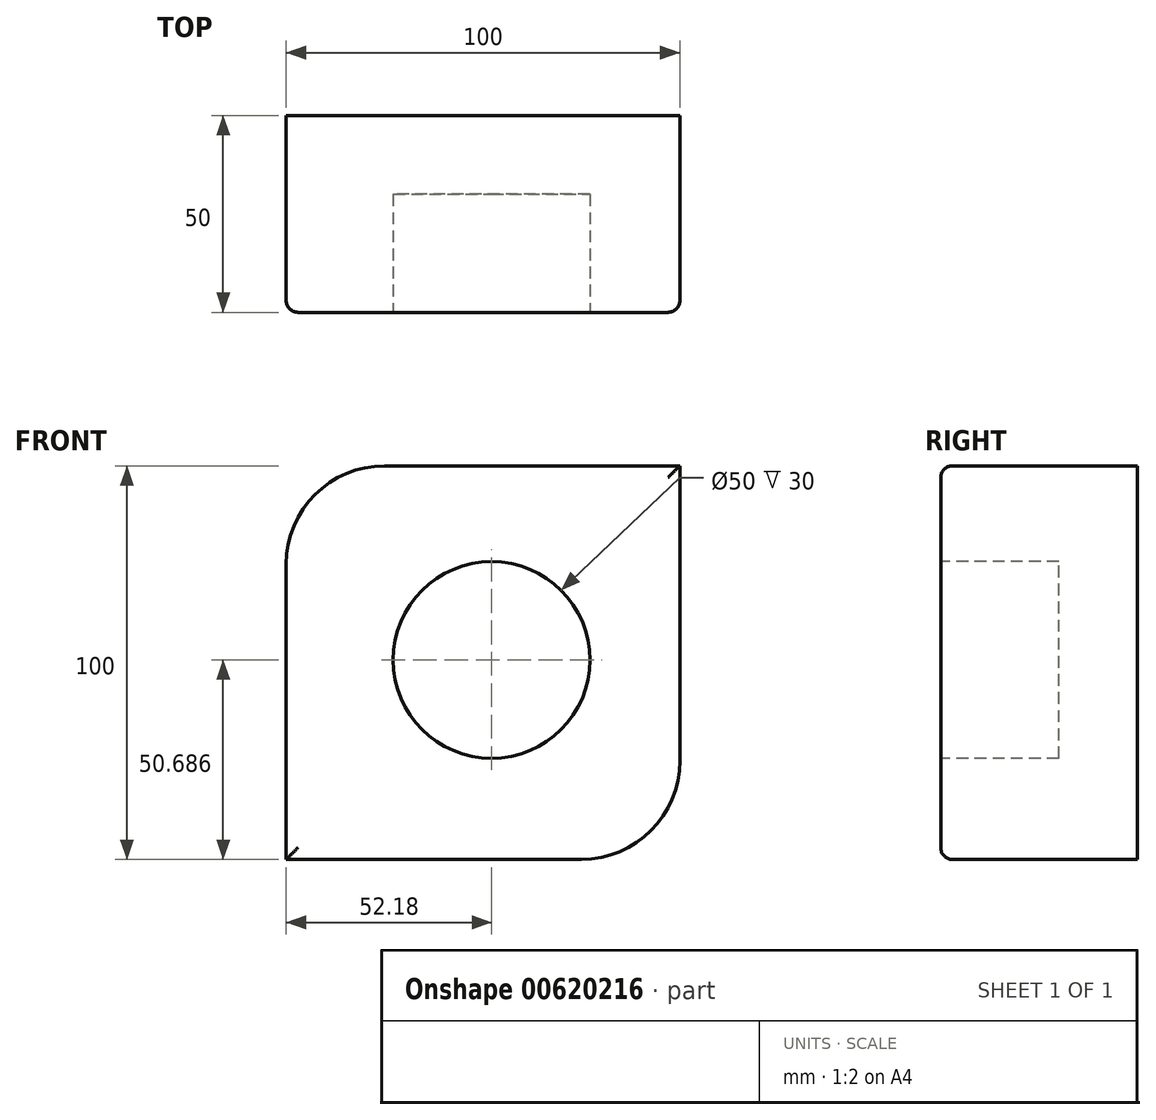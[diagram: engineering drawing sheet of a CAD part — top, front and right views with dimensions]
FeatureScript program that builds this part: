
annotation { "Feature Type Name" : "Feature", "Feature Type Description" : "" }
export const myFeature = defineFeature(function(context is Context, id is Id, definition is map)
    precondition{}
    {
        {
            var Q0;
            Q0=qCreatedBy(makeId("Front.planeOp"),FACE);
            var sketch = newSketch(context, id + "F0", { "sketchPlane" : qUnion([Q0])});
            skLineSegment(sketch, "E0.bottom", {"start": v(-20.42, 67.46) * mm, "end": v(54.58, 67.46) * mm});
            skLineSegment(sketch, "E0.top", {"start": v(-45.42, -32.54) * mm, "end": v(29.58, -32.54) * mm});
            skLineSegment(sketch, "E0.left", {"start": v(-45.42, 42.46) * mm, "end": v(-45.42, -32.54) * mm});
            skLineSegment(sketch, "E0.right", {"start": v(54.58, 67.46) * mm, "end": v(54.58, -7.54) * mm});
            skPoint(sketch, "E1.visualSharp", {"position": v(-45.42, 67.46) * mm});
            skArc(sketch, "E1.filletArc", {"start": v(-20.42, 67.46) * mm, "mid": v(-38.1, 60.14) * mm, "end": v(-45.42, 42.46) * mm});
            skPoint(sketch, "E2.visualSharp", {"position": v(54.58, -32.54) * mm});
            skArc(sketch, "E2.filletArc", {"start": v(29.58, -32.54) * mm, "mid": v(47.25, -25.22) * mm, "end": v(54.58, -7.54) * mm});
            skSolve(sketch);
        }
        {
            var Q0;
            Q0=makeQuery(id+"F0.imprint","IMPRINT",FACE,{"disambiguationData":[TD([[makeQuery(id+"F0.imprint","IMPRINT",EDGE,{"derivedFrom":sQuery(id+"F0.wireOp",EDGE,"E0.bottom")}),-1.0]])]});
            extrude(context, id + "F1", {"entities" : qUnion([Q0]), "depth" : 50 * mm, "offsetDistance" : 25 * mm});
        }
        {
            var Q0;
            Q0=makeQuery(id+"F1.opExtrude","CAP_FACE",FACE,{"disambiguationData":[OSD([sQuery(id+"F0.wireOp",EDGE,"E0.bottom"),sQuery(id+"F0.wireOp",EDGE,"E0.top"),sQuery(id+"F0.wireOp",EDGE,"E0.left"),sQuery(id+"F0.wireOp",EDGE,"E0.right"),sQuery(id+"F0.wireOp",EDGE,"E1.filletArc"),sQuery(id+"F0.wireOp",EDGE,"E2.filletArc")])],"isStart":false});
            fillet(context, id + "F2", {"entities" : qUnion([Q0]), "radius" : 3 * mm, "tangentPropagation" : true, "allowEdgeOverflow" : false});
        }
        {
            var Q0;
            Q0=makeQuery(id+"F1.opExtrude","CAP_FACE",FACE,{"disambiguationData":[OSD([sQuery(id+"F0.wireOp",EDGE,"E0.bottom"),sQuery(id+"F0.wireOp",EDGE,"E0.top"),sQuery(id+"F0.wireOp",EDGE,"E0.left"),sQuery(id+"F0.wireOp",EDGE,"E0.right"),sQuery(id+"F0.wireOp",EDGE,"E1.filletArc"),sQuery(id+"F0.wireOp",EDGE,"E2.filletArc")])],"isStart":false});
            var sketch = newSketch(context, id + "F3", { "sketchPlane" : qUnion([Q0])});
            skCircle(sketch, "E3", {"center": v(6.76, 18.15) * mm, "radius": 25 * mm});
            skSolve(sketch);
        }
        {
            var Q0;
            Q0=makeQuery(id+"F3.imprint","IMPRINT",FACE,{"disambiguationData":[TD([[makeQuery(id+"F3.imprint","IMPRINT",EDGE,{"derivedFrom":sQuery(id+"F3.wireOp",EDGE,"E3")}),1.0]])]});
            extrude(context, id + "F4", {"entities" : qUnion([Q0]), "operationType" : NewBodyOperationType.REMOVE, "oppositeDirection" : true, "depth" : 30 * mm, "offsetDistance" : 25 * mm});
        }
    });
